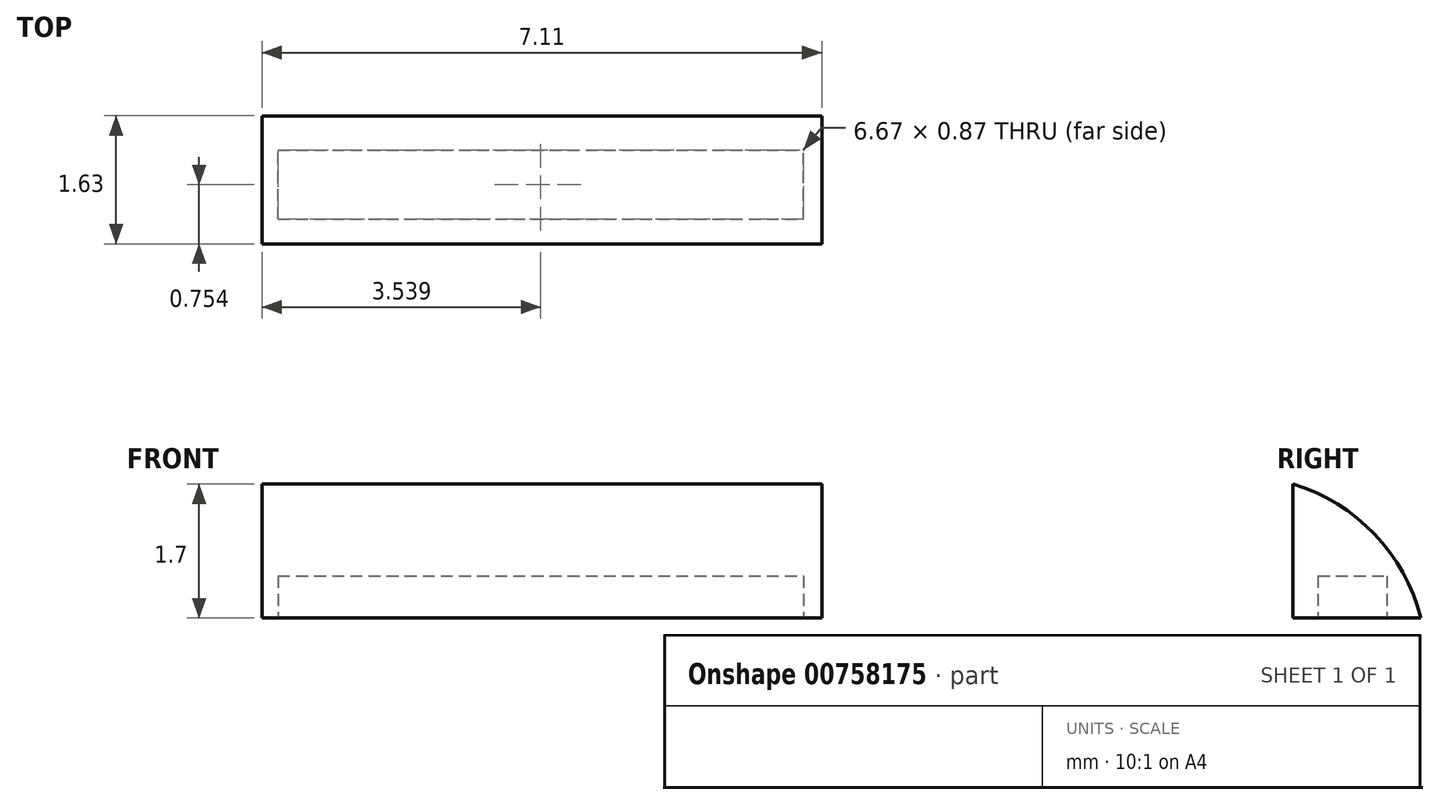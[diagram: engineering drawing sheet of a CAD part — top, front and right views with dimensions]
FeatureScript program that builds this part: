
annotation { "Feature Type Name" : "Feature", "Feature Type Description" : "" }
export const myFeature = defineFeature(function(context is Context, id is Id, definition is map)
    precondition{}
    {
        {
            var Q0;
            Q0=qCreatedBy(makeId("Front.planeOp"),FACE);
            var sketch = newSketch(context, id + "F0", { "sketchPlane" : qUnion([Q0])});
            skLineSegment(sketch, "E0.bottom", {"start": v(-63.55, 50.5) * mm, "end": v(-56.44, 50.5) * mm});
            skLineSegment(sketch, "E0.top", {"start": v(-63.55, 48.69) * mm, "end": v(-56.44, 48.69) * mm});
            skLineSegment(sketch, "E0.left", {"start": v(-63.55, 50.5) * mm, "end": v(-63.55, 48.69) * mm});
            skLineSegment(sketch, "E0.right", {"start": v(-56.44, 50.5) * mm, "end": v(-56.44, 48.69) * mm});
            skSolve(sketch);
        }
        {
            var Q0;
            Q0 = qSketchRegion(id + "F0", true);
            extrude(context, id + "F1", {"entities" : qUnion([Q0]), "oppositeDirection" : true, "depth" : 1.63 * mm, "offsetDistance" : 25.4 * mm});
        }
        {
            var Q0;
            Q0=makeQuery(id+"F1.opExtrude","CAP_EDGE",EDGE,{"disambiguationData":[OSD([sQuery(id+"F0.wireOp",EDGE,"E0.bottom")])],"isStart":false});
            fillet(context, id + "F2", {"entities" : qUnion([Q0]), "radius" : 2.4 * mm, "tangentPropagation" : true, "allowEdgeOverflow" : false});
        }
        {
            var Q0;
            Q0=makeQuery(id+"F1.opExtrude","SWEPT_FACE",FACE,{"disambiguationData":[OSD([sQuery(id+"F0.wireOp",EDGE,"E0.top")])]});
            var sketch = newSketch(context, id + "F3", { "sketchPlane" : qUnion([Q0])});
            skLineSegment(sketch, "E1.bottom", {"start": v(-63.35, -0.32) * mm, "end": v(-56.67, -0.32) * mm});
            skLineSegment(sketch, "E1.top", {"start": v(-63.35, -1.2) * mm, "end": v(-56.67, -1.2) * mm});
            skLineSegment(sketch, "E1.left", {"start": v(-63.35, -0.32) * mm, "end": v(-63.35, -1.2) * mm});
            skLineSegment(sketch, "E1.right", {"start": v(-56.67, -0.32) * mm, "end": v(-56.67, -1.2) * mm});
            skSolve(sketch);
        }
        {
            var Q0;
            Q0=makeQuery(id+"F3.imprint","IMPRINT",FACE,{"disambiguationData":[TD([[makeQuery(id+"F3.imprint","IMPRINT",EDGE,{"derivedFrom":sQuery(id+"F3.wireOp",EDGE,"E1.bottom")}),-1.0]])]});
            extrude(context, id + "F4", {"entities" : qUnion([Q0]), "operationType" : NewBodyOperationType.REMOVE, "oppositeDirection" : true, "depth" : 0.53 * mm, "offsetDistance" : 25.4 * mm});
        }
    });
